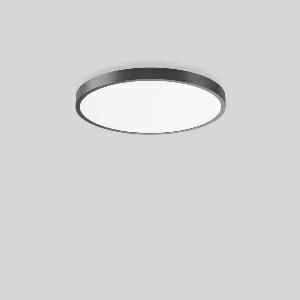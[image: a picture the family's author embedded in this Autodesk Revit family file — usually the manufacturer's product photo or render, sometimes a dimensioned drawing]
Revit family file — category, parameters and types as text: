
# Revit family: triona_round_a_312383_0031_76_82c1
name_source: partatom
category: Lighting Fixtures
units: mm (PartAtom-declared; Revit-internal decimal feet)

## family parameters
Cut with Voids When Loaded = No
Host = Face
Light Source = No
Part Type = Normal
Room Calculation Point = No
Round Connector Dimension = Use Diameter
Shared = No

## types (1)
- TRIONA round A (1 x LED Modul 830, 6450 lm, 3000)
    Apparent Load = 70 VA
    CIE Flux Codes = 49 80 96 100 100
    Color Rendering = 80
    Color Temperature = 3000
    Default Elevation = 1800 mm
    Description = Series: TRIONA round
Decorative round LED surface-mounted luminaire. Flat, seamless frame: aluminium extrusion profile, powder coated. Cover made of sheet steel, powder-coated. Light emission through a diffuser: plastic, opal. Lightguide and diffuser made of non-yellowing plastic (PMMA). Lateral light emission (RZB SIDELITE technology) for above-average homogeneous light distribution. Suitable for Ceiling mounting, Wall (surface). Tool-free mounting via bayonet connection. Electronic ballast included. Very easy installation thanks to Plug+Play connection. 
Colour: anthracite metallic (DB703)
Diameter: 681 mm
Height: 88 mm
Lamp: LED
Socket: without socket
Colour temperature: 3000K
Colour rendering index (CRI): 80
System power: 70 W
Rated luminous flux: 6450 lm
Luminous efficiency: 92 lm/W
Control gear: Converter, dimmable, DALI
Protection class: I
Type of protection: IP 20
    Height = 88 mm
    Lamp = 1 x LED Modul 830
    Lamp Light Flux = 6450 lm
    Lamp count = 1
    Length = 681 mm
    Lifetime = 50000 h
    Luminous efficacy = 92 lm/W
    Manufacturer = RZB
    ModVariant = No
    Model = 312383.0031.76
    Mounting Place = Ceiling
    Mounting Type = Surface mounted
    Number of Poles = 1
    OnlyDefault = Yes
    Power Factor = 1
    Product Name = TRIONA round A
    Product group = Surface mounted modular luminaires
    ProductGroupID = 306
    Protection Class = Protection class I
    Protection Degree = IP 20
    RLX_Detail_Level = 1
    RLX_Emergency_Light_Flux = 0 lm
    RLX_Emergency_Type = 0
    RLX_Emergency_Type_DB = No
    RlxData = <blob elided: 33997 chars, md5=9cfba122>
    Socket = socket
    Standby Power = 0 W
    System Light Flux = 6450 lm
    System Power = 70 W
    Type Comments = Product without accessories
    Type Image = 312384.0031.jpg
    URL = http://relux.com
    VarID = ---
    Voltage = 230 V
    Voltage Range = 220-240 V
    Weight = 0.00 kg
    Width = 0 mm  [stored 0 ft]

note: [stored X ft] marks values corroborated as IEEE doubles in the binary element streams (Revit-internal decimal feet)

## geometry (parser evidence)
native form markers: Blend x4, Sweep x10
no freeform markers — native parametric forms only
